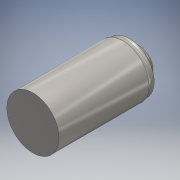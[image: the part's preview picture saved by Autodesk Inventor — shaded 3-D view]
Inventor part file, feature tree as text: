
AUTODESK INVENTOR PART (.ipt)
format: ipt  version: 2016 (Build 200138000, 138)  size: 196,608 bytes
history: native  units: mm
features: sketch x10, extrude x5, plane x4, fillet x4, loft x3, other x2
ambient origin geometry x8: Origin, YZ Plane, XZ Plane, XY Plane, X Axis, Y Axis, Z Axis, Center Point
bodies: Solid1 (feature_tree)
feature tree (28):
  extrude  "Extrusion1"  Depth=100.0mm TaperAngle=0.0deg
  plane  "Work Plane1"
  sketch  "Sketch2"  dims[d3=7.0mm d4=55.5mm]
  plane  "Work Plane2"
  loft  "Loft1"
  plane  "Work Plane4"
  loft  "Loft2"
  loft  "Loft3"
  fillet  "Fillet1"  [1 undecoded]
  extrude  "Extrusion2"  Depth=12.0mm
  fillet  "Fillet2"  [1 undecoded]
  extrude  "Extrusion3"  Depth=32.5mm
  fillet  "Fillet3"  Radius=32.5mm
  extrude  "Extrusion4"  TaperAngle=0.0deg  [1 undecoded]
  fillet  "Fillet4"  Radius=2.0mm
  extrude  "Extrusion5"  Depth=8.0mm TaperAngle=0.0deg
  sketch  "Sketch1"  dims[d0=58.0mm d1=100.0mm d2=0.0mm]
  sketch  "Sketch3"  dims[d5=3.5mm d6=53.5mm]
  other  "Edges1"
  plane  "Work Plane3"
  sketch  "Sketch4"  dims[d7=0.0mm d8=90.0deg d9=0.0mm d10=90.0deg d11=0.0mm d12=90.0deg]
  other  "Edges2"
  sketch  "Sketch5"  dims[d13=12.0mm d14=-4.5mm d15=30.0mm d16=0.0mm d17=90.0deg]
  sketch  "Sketch6"  dims[d18=0.0mm d19=90.0deg d20=32.5mm d21=32.5mm]
  sketch  "Sketch7"  dims[d22=0.0mm d23=90.0deg d24=0.0mm d25=90.0deg d26=2.0mm]
  sketch  "Sketch8"  dims[d27=24.0mm d28=8.0mm d29=0.0mm]
  sketch  "Sketch9"  dims[d30=2.0mm]
  sketch  "Sketch10"  dims[d31=10.5mm d32=8.0mm d33=0.0mm d34=1.0mm d35=4.0mm d36=7.7mm d37=0.0mm d38=0.5mm d39=7.7mm d40=0.0mm]
note: 3 required parameter values undecoded (feature->parameter linkage not recoverable at this tier; creation-order binding heuristic only, values carry confidence <= 0.55)
